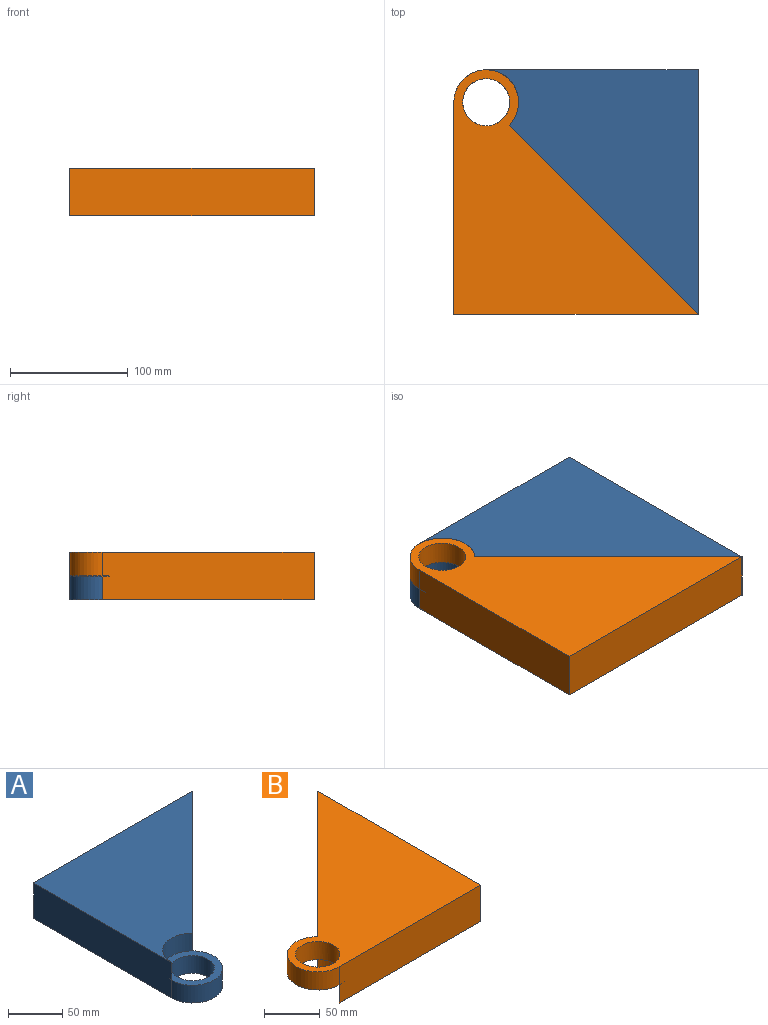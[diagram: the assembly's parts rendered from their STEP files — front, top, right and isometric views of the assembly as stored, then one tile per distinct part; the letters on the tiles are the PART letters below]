
ASSEMBLY  parts=2 mates=1
PART A: 9 faces, bbox 207.5x207.5x40 mm
  f0: cylinder r=27.5mm len=55mm, axis (0,0,-1), area 2159.8mm2, adj f2,f3,f6,f8
  f1: cylinder r=20mm len=40mm, axis (0,0,-1), area 2513.3mm2, adj f6,f8
  f2: plane 180x40mm, normal (-1,0,0), area 7200mm2, adj f0,f4,f5,f6,f7
  f3: plane 160.55x160.55mm, normal (0.71,-0.71,0), area 9082.3mm2, adj f0,f4,f5,f6,f7
  f4: plane 207.5x40mm, normal (0,1,0), area 8300mm2, adj f2,f3,f5,f6
  f5: plane 207.5x180mm, normal (0,0,1), area 20259.1mm2, adj f2,f3,f4,f7
  f6: plane 207.5x207.5mm, normal (0,0,-1), area 21378.3mm2, adj f0,f1,f2,f3,f4
  f7: cylinder r=27.5mm len=46.95mm, axis (0,0,1), area 1295.9mm2, adj f2,f3,f5,f8
  f8: plane 55x55mm, normal (0,0,1), area 1119.2mm2, adj f0,f1,f7
PART B: 9 faces, bbox 207.5x207.5x40 mm
  f0: cylinder r=20mm len=40mm, axis (0,0,-1), area 2513.3mm2, adj f5,f8
  f1: plane 180x40mm, normal (0,-1,0), area 7200mm2, adj f2,f4,f5,f6,f7
  f2: plane 207.5x40mm, normal (1,0,0), area 8300mm2, adj f1,f3,f5,f6
  f3: plane 160.55x160.55mm, normal (-0.71,0.71,0), area 9082.3mm2, adj f2,f4,f5,f6,f7
  f4: cylinder r=27.5mm len=55mm, axis (0,0,-1), area 2159.8mm2, adj f1,f3,f5,f8
  f5: plane 207.5x207.5mm, normal (0,0,1), area 21378.3mm2, adj f0,f1,f2,f3,f4
  f6: plane 207.5x180mm, normal (0,0,-1), area 20259.1mm2, adj f1,f2,f3,f7
  f7: cylinder r=27.5mm len=46.95mm, axis (0,0,-1), area 1295.9mm2, adj f1,f3,f6,f8
  f8: plane 55x55mm, normal (0,0,-1), area 1119.2mm2, adj f0,f4,f7
PLACE A rot(axis=(0,0,-1),90deg) t=(161.06,269.02,20.37)mm
PLACE B rot(axis=(0,0,-1),90deg) t=(180,190.43,20.37)mm
MATE cylindrical B.f0 <-> A.f1  axis (0,0,1) through (161.06,269.02,60.37)mm
